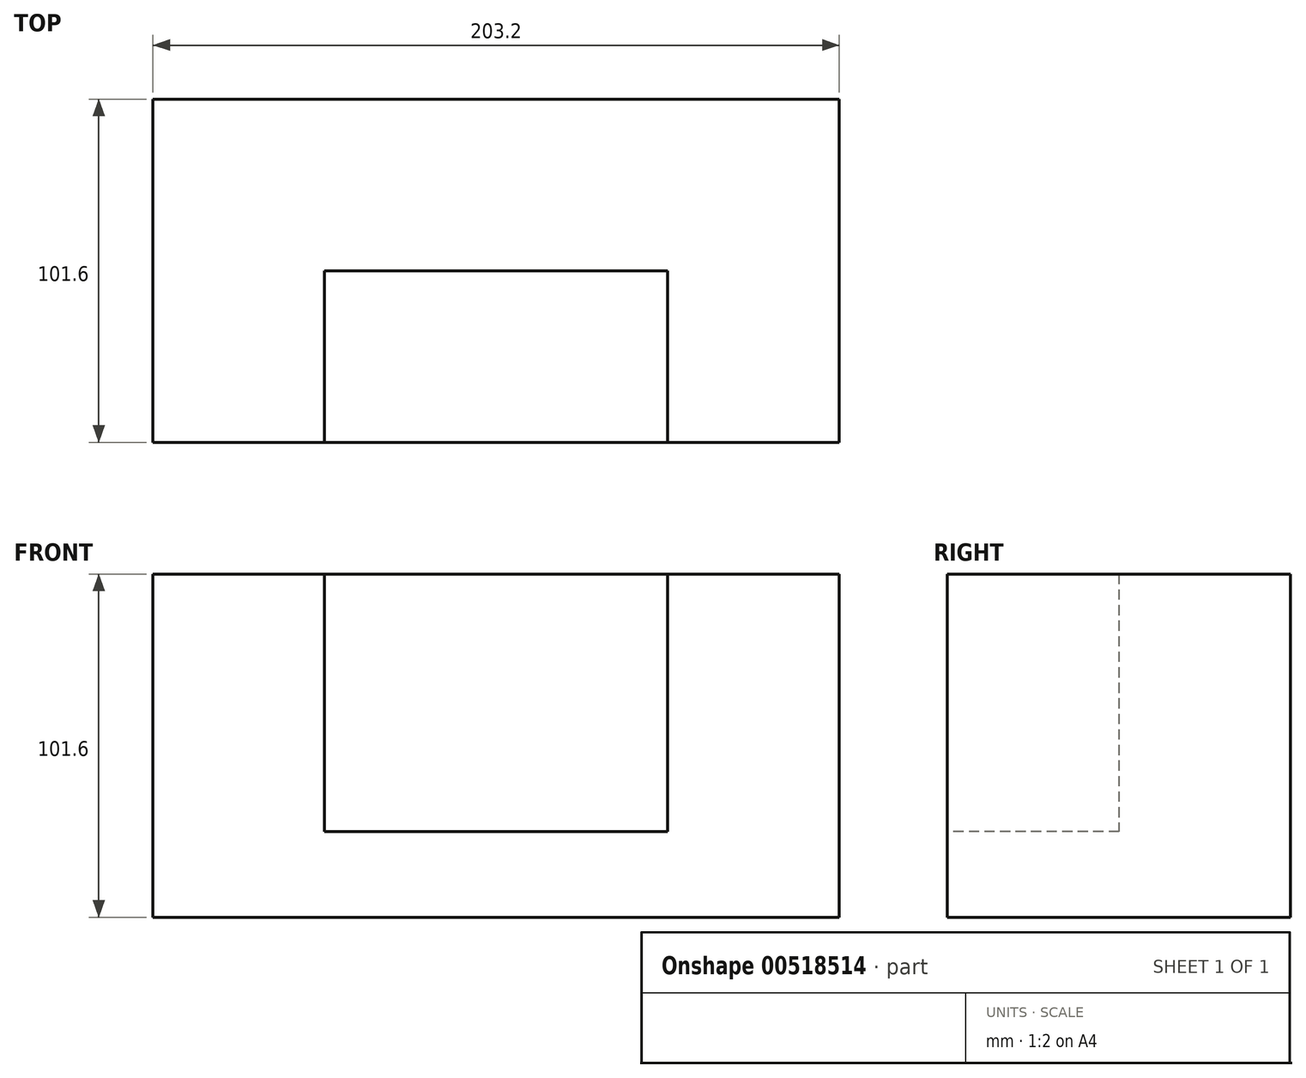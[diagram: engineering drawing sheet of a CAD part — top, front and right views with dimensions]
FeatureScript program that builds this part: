
annotation { "Feature Type Name" : "Feature", "Feature Type Description" : "" }
export const myFeature = defineFeature(function(context is Context, id is Id, definition is map)
    precondition{}
    {
        {
            var Q0;
            Q0=qCreatedBy(makeId("Front.planeOp"),FACE);
            var sketch = newSketch(context, id + "F0", { "sketchPlane" : qUnion([Q0])});
            skLineSegment(sketch, "E0.bottom", {"start": v(-101.31, 46.93) * mm, "end": v(101.89, 46.93) * mm});
            skLineSegment(sketch, "E0.top", {"start": v(-101.31, -54.67) * mm, "end": v(101.89, -54.67) * mm});
            skLineSegment(sketch, "E0.left", {"start": v(-101.31, 46.93) * mm, "end": v(-101.31, -54.67) * mm});
            skLineSegment(sketch, "E0.right", {"start": v(101.89, 46.93) * mm, "end": v(101.89, -54.67) * mm});
            skSolve(sketch);
        }
        {
            var Q0;
            Q0=qSketchRegion(id+"F0",true);
            extrude(context, id + "F1", {"entities" : qUnion([Q0]), "depth" : 101.6 * mm, "offsetDistance" : 25.4 * mm});
        }
        {
            var Q0;
            Q0=makeQuery(id+"F1.opExtrude","CAP_FACE",FACE,{"disambiguationData":[OSD([sQuery(id+"F0.wireOp",EDGE,"E0.bottom"),sQuery(id+"F0.wireOp",EDGE,"E0.top"),sQuery(id+"F0.wireOp",EDGE,"E0.left"),sQuery(id+"F0.wireOp",EDGE,"E0.right")])],"isStart":false});
            var sketch = newSketch(context, id + "F2", { "sketchPlane" : qUnion([Q0])});
            skLineSegment(sketch, "E1.bottom", {"start": v(-50.51, 46.93) * mm, "end": v(51.09, 46.93) * mm});
            skLineSegment(sketch, "E1.top", {"start": v(-50.51, -29.27) * mm, "end": v(51.09, -29.27) * mm});
            skLineSegment(sketch, "E1.left", {"start": v(-50.51, 46.93) * mm, "end": v(-50.51, -29.27) * mm});
            skLineSegment(sketch, "E1.right", {"start": v(51.09, 46.93) * mm, "end": v(51.09, -29.27) * mm});
            skSolve(sketch);
        }
        {
            var Q0;
            Q0=qSketchRegion(id+"F2",true);
            extrude(context, id + "F3", {"entities" : qUnion([Q0]), "operationType" : NewBodyOperationType.REMOVE, "oppositeDirection" : true, "depth" : 50.8 * mm, "offsetDistance" : 25.4 * mm});
        }
    });
